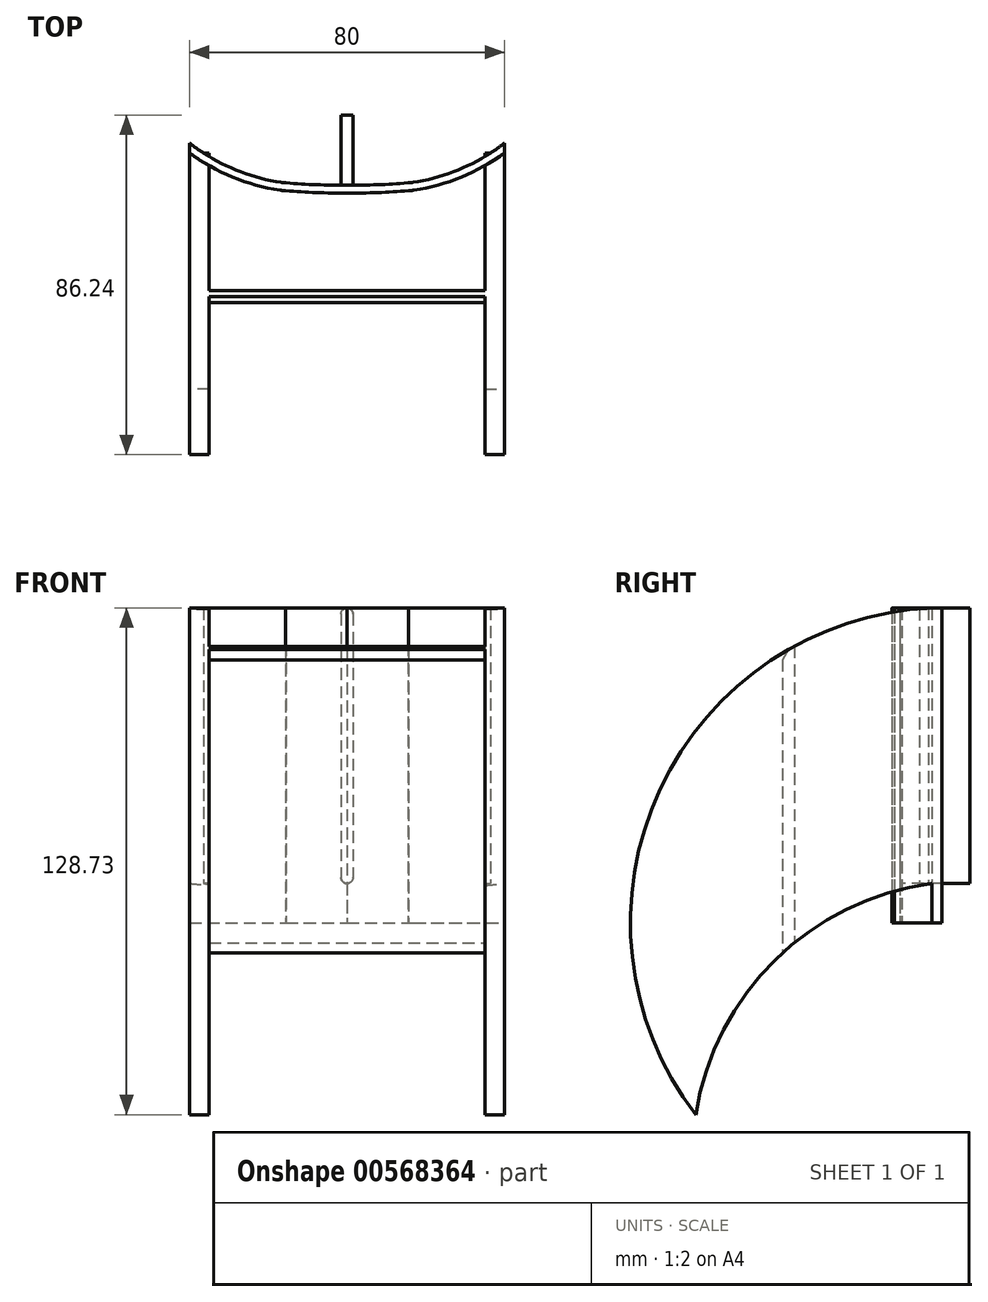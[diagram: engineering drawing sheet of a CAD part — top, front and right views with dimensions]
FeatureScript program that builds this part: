
annotation { "Feature Type Name" : "Feature", "Feature Type Description" : "" }
export const myFeature = defineFeature(function(context is Context, id is Id, definition is map)
    precondition{}
    {
        {
            var Q0;
            Q0=qCreatedBy(makeId("Top.planeOp"),FACE);
            var sketch = newSketch(context, id + "F0", { "sketchPlane" : qUnion([Q0])});
            skArc(sketch, "E0.0", {"start": v(-54.28, -34.06) * mm, "mid": v(-38.97, -52.6) * mm, "end": v(-16.74, -61.8) * mm});
            skArc(sketch, "E0.1", {"start": v(0.17, -62.47) * mm, "mid": v(-7.65, -62.4) * mm, "end": v(-15.45, -61.92) * mm});
            skArc(sketch, "E1", {"start": v(-16.74, -61.8) * mm, "mid": v(-16.1, -61.88) * mm, "end": v(-15.45, -61.92) * mm});
            skLineSegment(sketch, "E2", {"start": v(-40, -36.14) * mm, "end": v(-40, -67.51) * mm});
            skArc(sketch, "E3.0", {"start": v(0.21, -64.47) * mm, "mid": v(-7.7, -64.4) * mm, "end": v(-15.59, -63.92) * mm});
            skArc(sketch, "E3.1", {"start": v(-17.03, -63.78) * mm, "mid": v(-16.31, -63.87) * mm, "end": v(-15.59, -63.92) * mm});
            skArc(sketch, "E3.2", {"start": v(-56.09, -34.92) * mm, "mid": v(-40.16, -54.21) * mm, "end": v(-17.03, -63.78) * mm});
            skLineSegment(sketch, "E4", {"start": v(-56.09, -34.92) * mm, "end": v(-54.28, -34.06) * mm});
            skLineSegment(sketch, "E5.MirrorCS", {"start": v(56.09, -34.92) * mm, "end": v(54.28, -34.06) * mm});
            skLineSegment(sketch, "E6.MirrorCS", {"start": v(40, -36.14) * mm, "end": v(40, -67.51) * mm});
            skArc(sketch, "E7.MirrorCS", {"start": v(17.03, -63.78) * mm, "mid": v(16.31, -63.87) * mm, "end": v(15.59, -63.92) * mm});
            skArc(sketch, "E8.MirrorCS", {"start": v(16.74, -61.8) * mm, "mid": v(16.1, -61.88) * mm, "end": v(15.45, -61.92) * mm});
            skArc(sketch, "E9.MirrorCS", {"start": v(56.09, -34.92) * mm, "mid": v(40.16, -54.21) * mm, "end": v(17.03, -63.78) * mm});
            skArc(sketch, "E10.MirrorCS", {"start": v(-0.21, -64.47) * mm, "mid": v(7.7, -64.4) * mm, "end": v(15.59, -63.92) * mm});
            skArc(sketch, "E11.MirrorCS", {"start": v(-0.17, -62.47) * mm, "mid": v(7.65, -62.4) * mm, "end": v(15.45, -61.92) * mm});
            skArc(sketch, "E12.MirrorCS", {"start": v(54.28, -34.06) * mm, "mid": v(38.97, -52.6) * mm, "end": v(16.74, -61.8) * mm});
            skSolve(sketch);
        }
        {
            var Q0;
            {var subQ13=sQuery(id+"F0.wireOp",EDGE,"E1");Q0=makeQuery(id+"F0.imprint","IMPRINT",FACE,{"disambiguationData":[TD([[makeQuery(id+"F0.imprint","IMPRINT",EDGE,{"derivedFrom":subQ13}),-1.0]])]});}
            extrude(context, id + "F1", {"entities" : qUnion([Q0]), "depth" : 80 * mm, "offsetDistance" : 25 * mm});
        }
        {
            var Q0;
            Q0=makeQuery(id+"F1.opExtrude","SWEPT_FACE",FACE,{"disambiguationData":[OSD([sQuery(id+"F0.wireOp",EDGE,"E6.MirrorCS")])]});
            var sketch = newSketch(context, id + "F2", { "sketchPlane" : qUnion([Q0])});
            skArc(sketch, "E13", {"start": v(-54.33, 80) * mm, "mid": v(-123.45, 33.87) * mm, "end": v(-114.33, -48.73) * mm});
            skArc(sketch, "E14", {"start": v(-114.33, -48.73) * mm, "mid": v(-94.11, -9.37) * mm, "end": v(-54.33, 10) * mm});
            skLineSegment(sketch, "E15", {"start": v(-89.33, 70.26) * mm, "end": v(-89.33, -5.1) * mm});
            skLineSegment(sketch, "E16", {"start": v(-92.33, 68.53) * mm, "end": v(-92.33, -7.69) * mm});
            skSolve(sketch);
        }
        {
            var Q0;
            {var subQ0=sQuery(id+"F2.wireOp",EDGE,"E13");Q0=makeQuery(id+"F2.imprint","IMPRINT",FACE,{"disambiguationData":[TD([[makeQuery(id+"F2.imprint","IMPRINT",EDGE,{"derivedFrom":subQ0}),1.0]])]});}
            var Q1;
            {var subQ4=sQuery(id+"F2.wireOp",EDGE,"E15");Q1=makeQuery(id+"F2.imprint","IMPRINT",FACE,{"disambiguationData":[TD([[makeQuery(id+"F2.imprint","IMPRINT",EDGE,{"derivedFrom":subQ4}),1.0]])]});}
            var Q2;
            {var subQ0=sQuery(id+"F2.wireOp",EDGE,"E15");Q2=makeQuery(id+"F2.imprint","IMPRINT",FACE,{"disambiguationData":[TD([[makeQuery(id+"F2.imprint","IMPRINT",EDGE,{"derivedFrom":subQ0}),-1.0]])]});}
            extrude(context, id + "F3", {"entities" : qUnion([Q0, Q1, Q2]), "operationType" : NewBodyOperationType.ADD, "oppositeDirection" : true, "depth" : 5 * mm, "offsetDistance" : 25 * mm});
        }
        {
            var Q0;
            Q0=makeQuery(id+"F1.opExtrude","SWEPT_FACE",FACE,{"disambiguationData":[OSD([sQuery(id+"F0.wireOp",EDGE,"E2")])]});
            var sketch = newSketch(context, id + "F4", { "sketchPlane" : qUnion([Q0])});
            skArc(sketch, "E17.0", {"start": v(114.33, -48.73) * mm, "mid": v(94.11, -9.37) * mm, "end": v(54.33, 10) * mm});
            skArc(sketch, "E17.1", {"start": v(54.33, 80) * mm, "mid": v(123.45, 33.87) * mm, "end": v(114.33, -48.73) * mm});
            skLineSegment(sketch, "E18", {"start": v(54.33, 10) * mm, "end": v(54.33, 80) * mm});
            skSolve(sketch);
        }
        {
            var Q0;
            Q0=makeQuery(id+"F4.imprint","IMPRINT",FACE,{"disambiguationData":[TD([[makeQuery(id+"F4.imprint","IMPRINT",EDGE,{"derivedFrom":sQuery(id+"F4.wireOp",EDGE,"E17.0")}),-1.0]])]});
            extrude(context, id + "F5", {"entities" : qUnion([Q0]), "operationType" : NewBodyOperationType.ADD, "oppositeDirection" : true, "depth" : 5 * mm, "offsetDistance" : 25 * mm});
        }
        {
            var Q0;
            {var subQ0=sQuery(id+"F2.wireOp",EDGE,"E15");Q0=makeQuery(id+"F2.imprint","IMPRINT",FACE,{"disambiguationData":[TD([[makeQuery(id+"F2.imprint","IMPRINT",EDGE,{"derivedFrom":subQ0}),-1.0]])]});}
            var Q1;
            Q1=makeQuery(id+"F5.opExtrude","CAP_FACE",FACE,{"disambiguationData":[OSD([sQuery(id+"F4.wireOp",EDGE,"E17.0"),sQuery(id+"F4.wireOp",EDGE,"E17.1"),sQuery(id+"F4.wireOp",EDGE,"E18")])],"isStart":false});
            extrude(context, id + "F6", {"entities" : qUnion([Q0]), "operationType" : NewBodyOperationType.ADD, "endBound" : BoundingType.UP_TO_SURFACE, "oppositeDirection" : true, "depth" : 25 * mm, "endBoundEntityFace" : qUnion([Q1]), "offsetDistance" : 25 * mm});
        }
        {
            var Q0;
            Q0=makeQuery(id+"F6.opExtrude","SWEPT_EDGE",EDGE,{"disambiguationData":[OSD([sQuery(id+"F2.wireOp",EDGE,"E13"),sQuery(id+"F2.wireOp",EDGE,"E16")])]});
            chamfer(context, id + "F7", {"entities" : qUnion([Q0]), "width" : 3 * mm, "tangentPropagation" : true});
        }
        {
            var Q0;
            Q0=qCreatedBy(makeId("Front.planeOp"),FACE);
            cPlane(context, id + "F8", {"entities" : qUnion([Q0]), "cplaneType" : CPlaneType.OFFSET, "offset" : 62.7 * mm, "width" : 150 * mm, "height" : 150 * mm});
        }
        {
            var Q0;
            Q0=qCreatedBy(id+"F8.planeOp",FACE);
            var sketch = newSketch(context, id + "F9", { "sketchPlane" : qUnion([Q0])});
            skLineSegment(sketch, "E19.bottom", {"start": v(0, 10) * mm, "end": v(0, 10) * mm});
            skLineSegment(sketch, "E19.top", {"start": v(0, 80) * mm, "end": v(0, 80) * mm});
            skLineSegment(sketch, "E19.left", {"start": v(-1.5, 11.5) * mm, "end": v(-1.5, 78.5) * mm});
            skLineSegment(sketch, "E19.right", {"start": v(1.5, 11.5) * mm, "end": v(1.5, 78.5) * mm});
            skPoint(sketch, "E19.middle", {"position": v(0, 45) * mm});
            skPoint(sketch, "E20.visualSharp", {"position": v(1.5, 80) * mm});
            skArc(sketch, "E20.filletArc", {"start": v(1.5, 78.5) * mm, "mid": v(1.06, 79.56) * mm, "end": v(0, 80) * mm});
            skPoint(sketch, "E21.visualSharp", {"position": v(-1.5, 80) * mm});
            skArc(sketch, "E21.filletArc", {"start": v(0, 80) * mm, "mid": v(-1.06, 79.56) * mm, "end": v(-1.5, 78.5) * mm});
            skPoint(sketch, "E22.visualSharp", {"position": v(1.5, 10) * mm});
            skArc(sketch, "E22.filletArc", {"start": v(0, 10) * mm, "mid": v(1.06, 10.44) * mm, "end": v(1.5, 11.5) * mm});
            skPoint(sketch, "E23.visualSharp", {"position": v(-1.5, 10) * mm});
            skArc(sketch, "E23.filletArc", {"start": v(-1.5, 11.5) * mm, "mid": v(-1.06, 10.44) * mm, "end": v(0, 10) * mm});
            skSolve(sketch);
        }
        {
            var Q0;
            Q0=makeQuery(id+"F9.imprint","IMPRINT",FACE,{"disambiguationData":[TD([[makeQuery(id+"F9.imprint","IMPRINT",EDGE,{"derivedFrom":sQuery(id+"F9.wireOp",EDGE,"E19.left")}),-1.0]])]});
            extrude(context, id + "F10", {"entities" : qUnion([Q0]), "operationType" : NewBodyOperationType.ADD, "oppositeDirection" : true, "depth" : 18 * mm, "offsetDistance" : 25 * mm});
        }
    });
